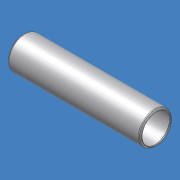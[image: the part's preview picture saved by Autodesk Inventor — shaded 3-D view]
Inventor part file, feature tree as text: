
AUTODESK INVENTOR PART (.ipt)
format: ipt  version: 2012 (Build 160160000, 160)  size: 117,760 bytes
history: native  units: mm (DEFAULTED — no unit token found)
features: other x42, revolve x1, sketch x1
ambient origin geometry x8: Origin, YZ Plane, XZ Plane, XY Plane, X Axis, Y Axis, Z Axis, Center Point
bodies: Solid1 (feature_tree)
feature tree (44):
  revolve  "Revolution1"  [1 undecoded]
  other  "tube_front_XY"
  other  "tube_front_YZ"
  other  "tube_front_ZX"
  other  "tube_front_X"
  other  "tube_front_Y"
  other  "tube_front_Z"
  other  "tube_front_Center"
  other  "tube_rear_XY"
  other  "tube_rear_YZ"
  other  "tube_rear_ZX"
  other  "tube_rear_X"
  other  "tube_rear_Y"
  other  "tube_rear_Z"
  other  "tube_rear_Center"
  other  "cp1_XY"
  other  "cp1_YZ"
  other  "cp1_ZX"
  other  "cp1_X"
  other  "cp1_Y"
  other  "cp1_Z"
  other  "cp1_Center"
  other  "cp2_XY"
  other  "cp2_YZ"
  other  "cp2_ZX"
  other  "cp2_X"
  other  "cp2_Y"
  other  "cp2_Z"
  other  "cp2_Center"
  other  "cp3_XY"
  other  "cp3_YZ"
  other  "cp3_ZX"
  other  "cp3_X"
  other  "cp3_Y"
  other  "cp3_Z"
  other  "cp3_Center"
  other  "cp4_XY"
  other  "cp4_YZ"
  other  "cp4_ZX"
  other  "cp4_X"
  other  "cp4_Y"
  other  "cp4_Z"
  other  "cp4_Center"
  sketch  "Sketch_1"  dims[d0=360.0deg]
note: 1 required parameter value undecoded (feature->parameter linkage not recoverable at this tier; creation-order binding heuristic only, values carry confidence <= 0.55)
